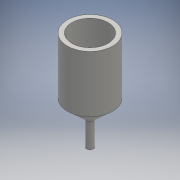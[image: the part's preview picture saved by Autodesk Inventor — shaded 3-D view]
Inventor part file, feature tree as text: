
AUTODESK INVENTOR PART (.ipt)
format: ipt  version: 2016 (Build 200138000, 138)  size: 108,032 bytes
history: native  units: mm
features: revolve x2, sketch x2, other x1, shell x1
ambient origin geometry x8: Origin, YZ Plane, XZ Plane, XY Plane, X Axis, Y Axis, Z Axis, Center Point
bodies: Body1 (feature_tree)
feature tree (6):
  other  "ソリッド1"
  revolve  "回転1"
  shell  "シェル1"  Thickness=50.0mm
  revolve  "回転2"
  sketch  "スケッチ1"
  sketch  "スケッチ2"
